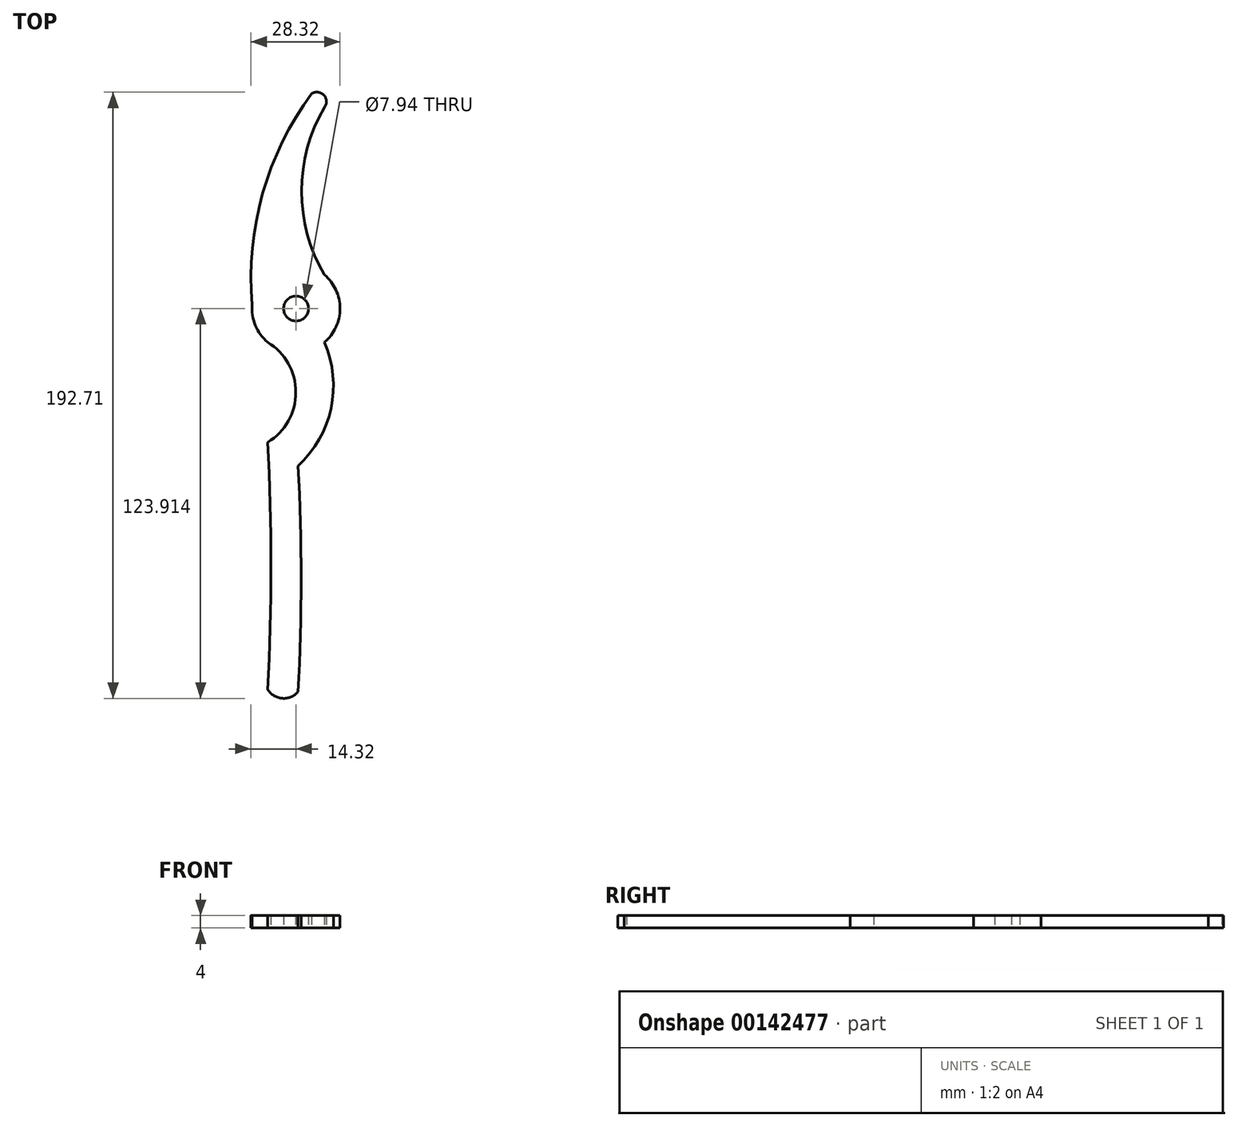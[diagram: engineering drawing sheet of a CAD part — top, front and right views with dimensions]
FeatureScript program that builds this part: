
annotation { "Feature Type Name" : "Feature", "Feature Type Description" : "" }
export const myFeature = defineFeature(function(context is Context, id is Id, definition is map)
    precondition{}
    {
        {
            var Q0;
            Q0=qCreatedBy(makeId("Top.planeOp"),FACE);
            var sketch = newSketch(context, id + "F0", { "sketchPlane" : qUnion([Q0])});
            skArc(sketch, "E0", {"start": v(-18, -31.8) * mm, "mid": v(-9.08, -15.9) * mm, "end": v(-18, 0) * mm});
            skArc(sketch, "E1", {"start": v(-8.38, -39.3) * mm, "mid": v(2.12, -21) * mm, "end": v(0, 0) * mm});
            skArc(sketch, "E2", {"start": v(-18, -110.4) * mm, "mid": v(-17, -71.1) * mm, "end": v(-18, -31.8) * mm});
            skArc(sketch, "E3", {"start": v(-8.38, -111.1) * mm, "mid": v(-7.37, -75.2) * mm, "end": v(-8.38, -39.3) * mm});
            skArc(sketch, "E4", {"start": v(-18, -110.4) * mm, "mid": v(-13.37, -113.18) * mm, "end": v(-8.38, -111.1) * mm});
            skLineSegment(sketch, "E5", {"start": v(0, 0) * mm, "end": v(-18, 0) * mm});
            skCircle(sketch, "E6", {"center": v(-9, 10.72) * mm, "radius": 3.97 * mm});
            skCircle(sketch, "E7", {"center": v(-9, 10.72) * mm, "radius": 14 * mm});
            skArc(sketch, "E8", {"start": v(0, 74.65) * mm, "mid": v(-7.25, 48.05) * mm, "end": v(0, 21.45) * mm});
            skArc(sketch, "E9", {"start": v(-4.03, 79) * mm, "mid": v(-19.64, 47.24) * mm, "end": v(-22.94, 12) * mm});
            skArc(sketch, "E10", {"start": v(0, 74.65) * mm, "mid": v(-0.14, 78.56) * mm, "end": v(-4.03, 79) * mm});
            skSolve(sketch);
        }
        {
            var Q0;
            {var subQ0=sQuery(id+"F0.wireOp",EDGE,"258f25f0-73f1-488b-a3a2-c2cd9996d2ce");Q0=makeQuery(id+"F0.imprint","IMPRINT",FACE,{"disambiguationData":[TD([[makeQuery(id+"F0.imprint","IMPRINT",EDGE,{"derivedFrom":subQ0}),-1.0]])]});}
            var Q1;
            {var subQ1=sQuery(id+"F0.wireOp",EDGE,"E5");Q1=makeQuery(id+"F0.imprint","IMPRINT",FACE,{"disambiguationData":[TD([[makeQuery(id+"F0.imprint","IMPRINT",EDGE,{"derivedFrom":subQ1}),-1.0]])]});}
            var Q2;
            {var subQ1=sQuery(id+"F0.wireOp",EDGE,"E1");Q2=makeQuery(id+"F0.imprint","IMPRINT",FACE,{"disambiguationData":[TD([[makeQuery(id+"F0.imprint","IMPRINT",EDGE,{"derivedFrom":subQ1}),1.0]])]});}
            var Q3;
            {var subQ1=sQuery(id+"F0.wireOp",EDGE,"E5");Q3=makeQuery(id+"F0.imprint","IMPRINT",FACE,{"disambiguationData":[TD([[makeQuery(id+"F0.imprint","IMPRINT",EDGE,{"derivedFrom":subQ1}),1.0]])]});}
            var Q4;
            {var subQ0=sQuery(id+"F0.wireOp",EDGE,"E8");Q4=makeQuery(id+"F0.imprint","IMPRINT",FACE,{"disambiguationData":[TD([[makeQuery(id+"F0.imprint","IMPRINT",EDGE,{"derivedFrom":subQ0}),-1.0]])]});}
            extrude(context, id + "F1", {"entities" : qUnion([Q0, Q1, Q2, Q3, Q4]), "depth" : 4 * mm});
        }
    });
